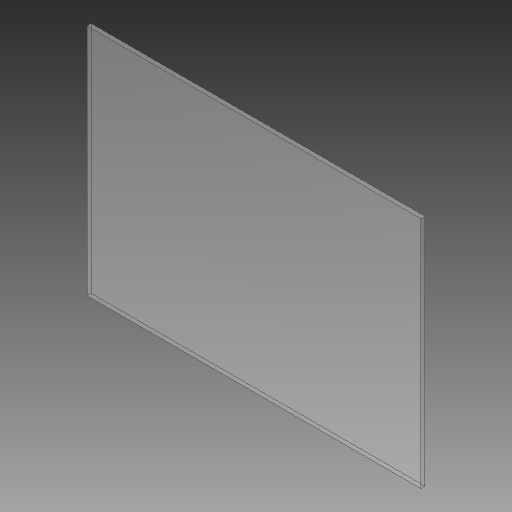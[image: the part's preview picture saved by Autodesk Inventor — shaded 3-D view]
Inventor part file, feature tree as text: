
AUTODESK INVENTOR PART (.ipt)
format: ipt  version: 2017 SP1 (Build 210196100, 196)  size: 94,720 bytes
history: native  units: in
note: dims shown in document units (in); Inventor stores cm internally (conversion verified against a paired STEP export)
features: extrude x1, sketch x1
ambient origin geometry x8: Origin, YZ Plane, XZ Plane, XY Plane, X Axis, Y Axis, Z Axis, Center Point
bodies: Solid1 (feature_tree)
feature tree (2):
  extrude  "Extrusion1"  Depth=7.0in
  sketch  "Sketch1"  dims[d0=10.0in d1=7.0in d2=0.125in d3=0.0in]
